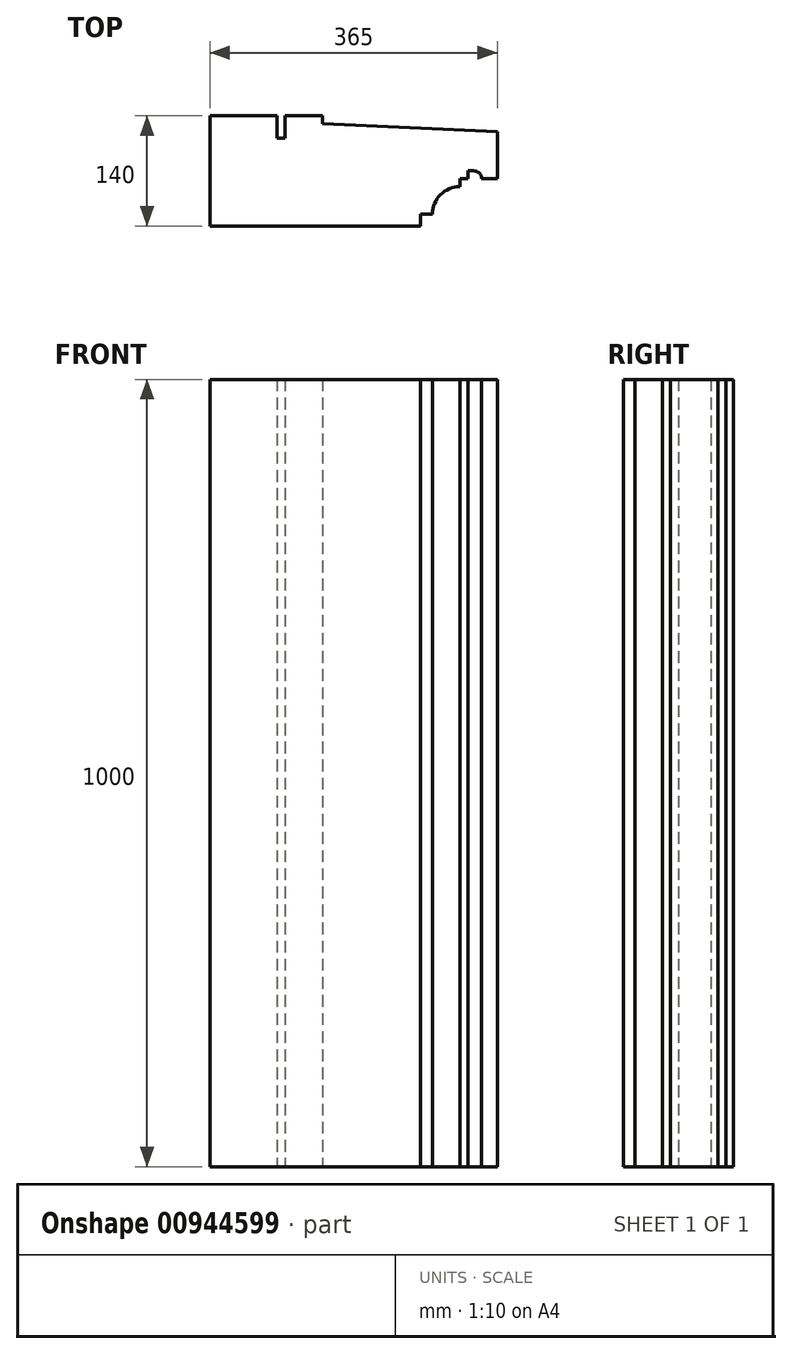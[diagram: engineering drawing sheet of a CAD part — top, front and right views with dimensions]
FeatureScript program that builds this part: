
annotation { "Feature Type Name" : "Feature", "Feature Type Description" : "" }
export const myFeature = defineFeature(function(context is Context, id is Id, definition is map)
    precondition{}
    {
        {
            var Q0;
            Q0=qCreatedBy(makeId("Top.planeOp"),FACE);
            var sketch = newSketch(context, id + "F0", { "sketchPlane" : qUnion([Q0])});
            skLineSegment(sketch, "E0", {"start": v(-172.32, 82.78) * mm, "end": v(-172.32, -57.22) * mm});
            skLineSegment(sketch, "E1", {"start": v(-172.32, -57.22) * mm, "end": v(95.18, -57.22) * mm});
            skLineSegment(sketch, "E2", {"start": v(95.18, -57.22) * mm, "end": v(95.18, -42.22) * mm});
            skLineSegment(sketch, "E3", {"start": v(95.18, -42.22) * mm, "end": v(110.18, -42.22) * mm});
            skLineSegment(sketch, "E4", {"start": v(-172.32, 82.78) * mm, "end": v(-87.32, 82.78) * mm});
            skLineSegment(sketch, "E5", {"start": v(-87.32, 82.78) * mm, "end": v(-87.32, 54.1) * mm});
            skLineSegment(sketch, "E6", {"start": v(-87.32, 54.1) * mm, "end": v(-77.32, 54.1) * mm});
            skLineSegment(sketch, "E7", {"start": v(-77.32, 54.1) * mm, "end": v(-77.32, 82.78) * mm});
            skLineSegment(sketch, "E8", {"start": v(-77.32, 82.78) * mm, "end": v(-29.32, 82.78) * mm});
            skLineSegment(sketch, "E9", {"start": v(-29.32, 82.78) * mm, "end": v(-29.32, 72.78) * mm});
            skLineSegment(sketch, "E10", {"start": v(-29.32, 72.78) * mm, "end": v(192.68, 62.78) * mm});
            skLineSegment(sketch, "E11", {"start": v(192.68, 62.78) * mm, "end": v(192.68, 2.78) * mm});
            skArc(sketch, "E12", {"start": v(110.18, -42.22) * mm, "mid": v(120.43, -17.47) * mm, "end": v(145.18, -7.22) * mm});
            skLineSegment(sketch, "E13", {"start": v(145.18, -7.22) * mm, "end": v(145.18, 2.78) * mm});
            skLineSegment(sketch, "E14", {"start": v(145.18, 2.78) * mm, "end": v(155.18, 2.78) * mm});
            skLineSegment(sketch, "E15", {"start": v(155.18, 2.78) * mm, "end": v(155.18, 12.78) * mm});
            skLineSegment(sketch, "E16", {"start": v(155.18, 12.78) * mm, "end": v(162.68, 12.78) * mm});
            skArc(sketch, "E17", {"start": v(162.68, 12.78) * mm, "mid": v(169.75, 9.85) * mm, "end": v(172.68, 2.78) * mm});
            skLineSegment(sketch, "E18", {"start": v(172.68, 2.78) * mm, "end": v(192.68, 2.78) * mm});
            skSolve(sketch);
        }
        {
            var Q0;
            Q0 = qSketchRegion(id + "F0", true);
            extrude(context, id + "F1", {"entities" : qUnion([Q0]), "depth" : 1000 * mm, "offsetDistance" : 25 * mm});
        }
    });
